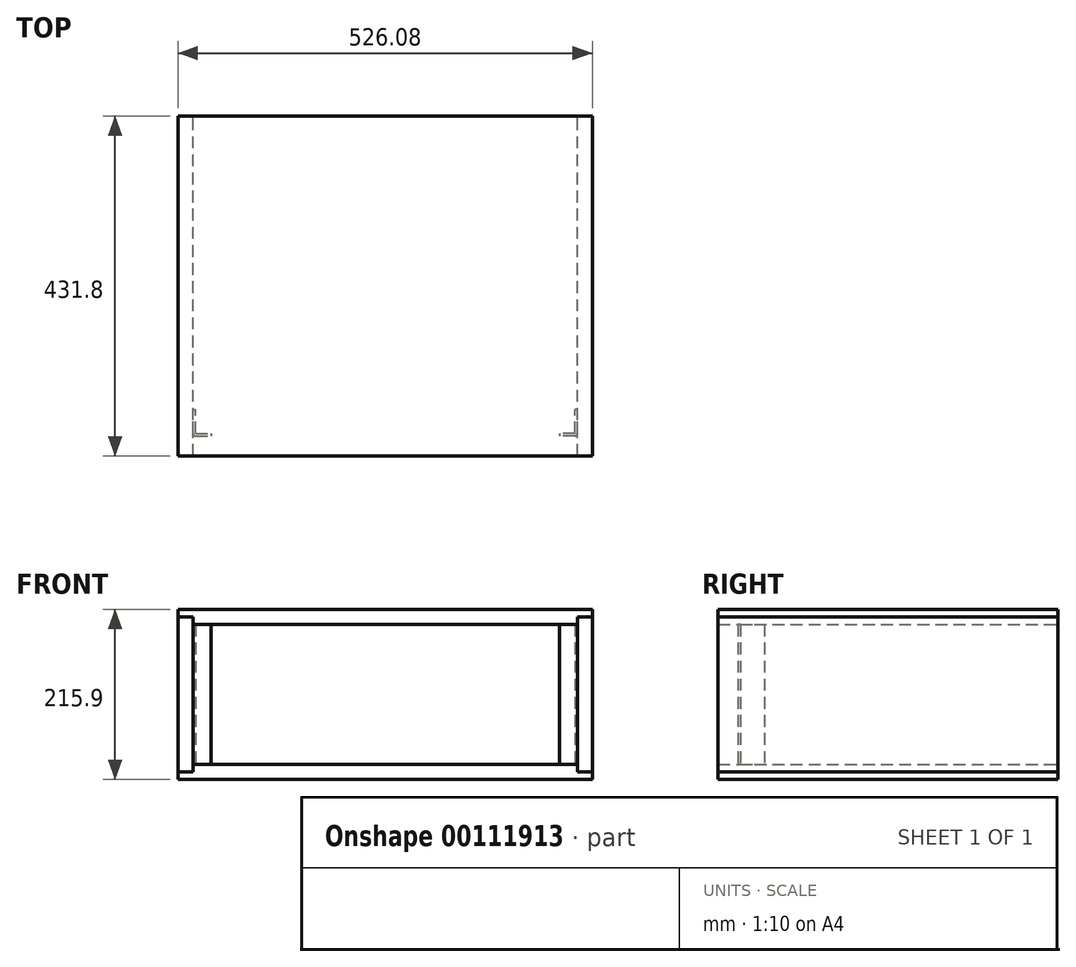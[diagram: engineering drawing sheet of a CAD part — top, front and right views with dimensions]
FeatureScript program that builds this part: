
annotation { "Feature Type Name" : "Feature", "Feature Type Description" : "" }
export const myFeature = defineFeature(function(context is Context, id is Id, definition is map)
    precondition{}
    {
        {
            var Q0;
            Q0=qCreatedBy(makeId("Top.planeOp"),FACE);
            var sketch = newSketch(context, id + "F0", { "sketchPlane" : qUnion([Q0])});
            skLineSegment(sketch, "E0", {"start": v(-244, 3.18) * mm, "end": v(-244, 33.34) * mm});
            skLineSegment(sketch, "E1", {"start": v(-240.82, 0) * mm, "end": v(-221.13, 0) * mm});
            skLineSegment(sketch, "E2", {"start": v(-232.56, 0) * mm, "end": v(-232.56, -23.2) * mm, "construction": true});
            skLineSegment(sketch, "E3", {"start": v(0, 0) * mm, "end": v(0, 140.19) * mm, "construction": true});
            skPoint(sketch, "E4.visualSharp", {"position": v(-244, 0) * mm});
            skArc(sketch, "E4.filletArc", {"start": v(-244, 3.18) * mm, "mid": v(-243.06, 0.93) * mm, "end": v(-240.82, 0) * mm});
            skLineSegment(sketch, "E5.0", {"start": v(-240.82, 3.18) * mm, "end": v(-240.82, 33.34) * mm});
            skLineSegment(sketch, "E5.1", {"start": v(-240.82, 3.18) * mm, "end": v(-221.13, 3.18) * mm});
            skLineSegment(sketch, "E6", {"start": v(-244, 33.34) * mm, "end": v(-240.82, 33.34) * mm});
            skLineSegment(sketch, "E7", {"start": v(-221.13, 3.18) * mm, "end": v(-221.13, 0) * mm});
            skArc(sketch, "E8.MirrorCS", {"start": v(244, 3.18) * mm, "mid": v(243.06, 0.93) * mm, "end": v(240.82, 0) * mm});
            skLineSegment(sketch, "E9.MirrorCS", {"start": v(221.13, 3.18) * mm, "end": v(221.13, 0) * mm});
            skLineSegment(sketch, "E10.MirrorCS", {"start": v(240.82, 0) * mm, "end": v(221.13, 0) * mm});
            skLineSegment(sketch, "E11.MirrorCS", {"start": v(244, 33.34) * mm, "end": v(240.82, 33.34) * mm});
            skLineSegment(sketch, "E12.MirrorCS", {"start": v(240.82, 3.18) * mm, "end": v(221.13, 3.18) * mm});
            skLineSegment(sketch, "E13.MirrorCS", {"start": v(244, 3.18) * mm, "end": v(244, 33.34) * mm});
            skLineSegment(sketch, "E14.MirrorCS", {"start": v(240.82, 3.18) * mm, "end": v(240.82, 33.34) * mm});
            skLineSegment(sketch, "E15.MirrorCS", {"start": v(232.56, 0) * mm, "end": v(232.56, -23.2) * mm, "construction": true});
            skPoint(sketch, "E16.MirrorP", {"position": v(244, 0) * mm});
            skSolve(sketch);
        }
        {
            var Q0;
            Q0 = qSketchRegion(id + "F0", true);
            extrude(context, id + "F1", {"entities" : qUnion([Q0]), "depth" : 177.8 * mm});
        }
        {
            var Q0;
            Q0=qCreatedBy(makeId("Front.planeOp"),FACE);
            var sketch = newSketch(context, id + "F2", { "sketchPlane" : qUnion([Q0])});
            skLineSegment(sketch, "E17", {"start": v(0, 0) * mm, "end": v(-244, 0) * mm, "construction": true});
            skLineSegment(sketch, "E18.0", {"start": v(-244, 177.8) * mm, "end": v(-244, 0) * mm});
            skLineSegment(sketch, "E19", {"start": v(-244, 0) * mm, "end": v(-263.04, 0) * mm, "construction": true});
            skLineSegment(sketch, "E20", {"start": v(-244, 177.8) * mm, "end": v(-263.04, 177.8) * mm, "construction": true});
            skLineSegment(sketch, "E21", {"start": v(-263.04, 177.8) * mm, "end": v(-263.04, 0) * mm});
            skLineSegment(sketch, "E22", {"start": v(-263.04, 0) * mm, "end": v(-263.04, -9.53) * mm});
            skLineSegment(sketch, "E23", {"start": v(-263.04, -9.53) * mm, "end": v(-244, -9.53) * mm});
            skLineSegment(sketch, "E24", {"start": v(-244, -9.53) * mm, "end": v(-244, 0) * mm});
            skLineSegment(sketch, "E25", {"start": v(-244, 177.8) * mm, "end": v(-244, 187.33) * mm});
            skLineSegment(sketch, "E26", {"start": v(-244, 187.33) * mm, "end": v(-263.04, 187.33) * mm});
            skLineSegment(sketch, "E27", {"start": v(-263.04, 187.33) * mm, "end": v(-263.04, 177.8) * mm});
            skLineSegment(sketch, "E28", {"start": v(0, 0) * mm, "end": v(0, 216.2) * mm, "construction": true});
            skLineSegment(sketch, "E29.MirrorCS", {"start": v(263.04, 0) * mm, "end": v(263.04, -9.53) * mm});
            skLineSegment(sketch, "E30.MirrorCS", {"start": v(244, -9.53) * mm, "end": v(244, 0) * mm});
            skLineSegment(sketch, "E31.MirrorCS", {"start": v(244, 177.8) * mm, "end": v(244, 187.33) * mm});
            skLineSegment(sketch, "E32.MirrorCS", {"start": v(263.04, 187.33) * mm, "end": v(263.04, 177.8) * mm});
            skLineSegment(sketch, "E33.MirrorCS", {"start": v(263.04, -9.53) * mm, "end": v(244, -9.53) * mm});
            skLineSegment(sketch, "E34.MirrorCS", {"start": v(244, 0) * mm, "end": v(263.04, 0) * mm, "construction": true});
            skLineSegment(sketch, "E35.MirrorCS", {"start": v(263.04, 177.8) * mm, "end": v(263.04, 0) * mm});
            skLineSegment(sketch, "E36.MirrorCS", {"start": v(244, 177.8) * mm, "end": v(263.04, 177.8) * mm, "construction": true});
            skLineSegment(sketch, "E37.MirrorCS", {"start": v(244, 187.33) * mm, "end": v(263.04, 187.33) * mm});
            skLineSegment(sketch, "E38.MirrorCS", {"start": v(244, 177.8) * mm, "end": v(244, 0) * mm});
            skLineSegment(sketch, "E39.MirrorCS", {"start": v(0, 0) * mm, "end": v(244, 0) * mm, "construction": true});
            skSolve(sketch);
        }
        {
            var Q0;
            Q0 = qSketchRegion(id + "F2", true);
            extrude(context, id + "F3", {"entities" : qUnion([Q0]), "depth" : 25.4 * mm, "hasSecondDirection" : true, "secondDirectionOppositeDirection" : true, "secondDirectionDepth" : 406.4 * mm});
        }
        {
            var Q0;
            Q0=qCreatedBy(makeId("Front.planeOp"),FACE);
            var sketch = newSketch(context, id + "F4", { "sketchPlane" : qUnion([Q0])});
            skLineSegment(sketch, "E40.0", {"start": v(-244, 187.33) * mm, "end": v(-263.04, 187.33) * mm});
            skLineSegment(sketch, "E41", {"start": v(-263.04, 187.33) * mm, "end": v(-263.04, 196.85) * mm});
            skLineSegment(sketch, "E42", {"start": v(-263.04, 196.85) * mm, "end": v(263.04, 196.85) * mm});
            skLineSegment(sketch, "E43.0", {"start": v(244, 187.33) * mm, "end": v(263.04, 187.33) * mm});
            skLineSegment(sketch, "E44", {"start": v(263.04, 187.33) * mm, "end": v(263.04, 196.85) * mm});
            skLineSegment(sketch, "E45", {"start": v(244, 187.33) * mm, "end": v(244, 177.8) * mm});
            skLineSegment(sketch, "E46", {"start": v(244, 177.8) * mm, "end": v(-244, 177.8) * mm});
            skLineSegment(sketch, "E47", {"start": v(-244, 177.8) * mm, "end": v(-244, 187.33) * mm});
            skLineSegment(sketch, "E48.0", {"start": v(221.13, 177.8) * mm, "end": v(221.13, 0) * mm, "construction": true});
            skLineSegment(sketch, "E49", {"start": v(221.13, 88.9) * mm, "end": v(-147.83, 88.9) * mm, "construction": true});
            skLineSegment(sketch, "E50.MirrorCS", {"start": v(-244, 0) * mm, "end": v(-244, -9.53) * mm});
            skLineSegment(sketch, "E51.MirrorCS", {"start": v(-263.04, -9.53) * mm, "end": v(-263.04, -19.05) * mm});
            skLineSegment(sketch, "E52.MirrorCS", {"start": v(244, -9.53) * mm, "end": v(263.04, -9.53) * mm});
            skLineSegment(sketch, "E53.MirrorCS", {"start": v(244, -9.53) * mm, "end": v(244, 0) * mm});
            skLineSegment(sketch, "E54.MirrorCS", {"start": v(263.04, -9.53) * mm, "end": v(263.04, -19.05) * mm});
            skLineSegment(sketch, "E55.MirrorCS", {"start": v(-244, -9.53) * mm, "end": v(-263.04, -9.53) * mm});
            skLineSegment(sketch, "E56.MirrorCS", {"start": v(221.13, 0) * mm, "end": v(221.13, 177.8) * mm, "construction": true});
            skLineSegment(sketch, "E57.MirrorCS", {"start": v(244, 0) * mm, "end": v(-244, 0) * mm});
            skLineSegment(sketch, "E58.MirrorCS", {"start": v(-263.04, -19.05) * mm, "end": v(263.04, -19.05) * mm});
            skSolve(sketch);
        }
        {
            var Q0;
            Q0=makeQuery(id+"F4.imprint","IMPRINT",FACE,{"disambiguationData":[TD([[makeQuery(id+"F4.imprint","IMPRINT",EDGE,{"derivedFrom":sQuery(id+"F4.wireOp",EDGE,"E50.MirrorCS")}),1.0]])]});
            var Q1;
            Q1=makeQuery(id+"F4.imprint","IMPRINT",FACE,{"disambiguationData":[TD([[makeQuery(id+"F4.imprint","IMPRINT",EDGE,{"derivedFrom":sQuery(id+"F4.wireOp",EDGE,"E40.0")}),-1.0]])]});
            var Q2;
            Q2=makeQuery(id+"F3.opExtrude","CAP_FACE",FACE,{"disambiguationData":[OSD([sQuery(id+"F2.wireOp",EDGE,"E18.0"),sQuery(id+"F2.wireOp",EDGE,"E21"),sQuery(id+"F2.wireOp",EDGE,"E22"),sQuery(id+"F2.wireOp",EDGE,"E23"),sQuery(id+"F2.wireOp",EDGE,"E24"),sQuery(id+"F2.wireOp",EDGE,"E25"),sQuery(id+"F2.wireOp",EDGE,"E26"),sQuery(id+"F2.wireOp",EDGE,"E27")])],"isStart":false});
            var Q3;
            Q3=makeQuery(id+"F3.opExtrude","CAP_FACE",FACE,{"disambiguationData":[OSD([sQuery(id+"F2.wireOp",EDGE,"E18.0"),sQuery(id+"F2.wireOp",EDGE,"E21"),sQuery(id+"F2.wireOp",EDGE,"E22"),sQuery(id+"F2.wireOp",EDGE,"E23"),sQuery(id+"F2.wireOp",EDGE,"E24"),sQuery(id+"F2.wireOp",EDGE,"E25"),sQuery(id+"F2.wireOp",EDGE,"E26"),sQuery(id+"F2.wireOp",EDGE,"E27")])],"isStart":true});
            extrude(context, id + "F5", {"entities" : qUnion([Q0, Q1]), "endBound" : BoundingType.UP_TO_SURFACE, "endBoundEntityFace" : qUnion([Q2]), "depth" : 25.4 * mm, "hasSecondDirection" : true, "secondDirectionBound" : SecondDirectionBoundingType.UP_TO_SURFACE, "secondDirectionOppositeDirection" : true, "secondDirectionBoundEntityFace" : qUnion([Q3]), "secondDirectionDepth" : 25.4 * mm});
        }
    });
